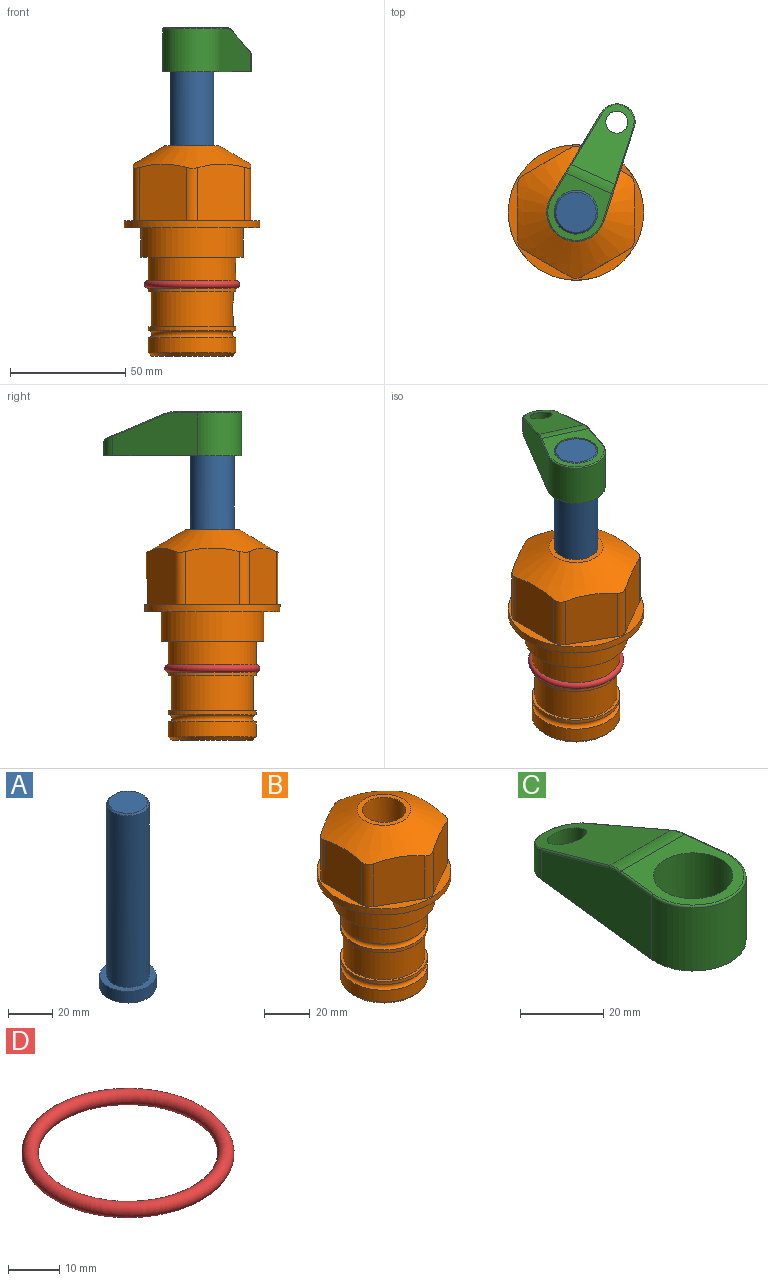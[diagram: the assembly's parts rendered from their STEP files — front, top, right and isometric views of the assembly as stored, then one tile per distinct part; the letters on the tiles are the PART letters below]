
ASSEMBLY  parts=4 mates=2
PART A: 6 faces, bbox 25.4x25.4x101.6 mm
  f0: plane 17.46x17.46mm, normal (0,0,1), area 239.5mm2, adj f5
  f1: plane 25.4x25.4mm, normal (0,0,-1), area 506.7mm2, adj f2
  f2: cylinder r=12.7mm len=25.4mm, axis (0,0,1), area 506.7mm2, adj f1,f3
  f3: plane 25.4x25.4mm, normal (0,0,1), area 221.7mm2, adj f2,f4
  f4: cylinder r=9.53mm len=94.46mm, axis (0,0,1), area 5653mm2, adj f3,f5
  f5: cone r=8.73mm half-angle=45deg, axis (0,0,-1), area 64.4mm2, adj f0,f4
PART B: 36 faces, bbox 58.7x58.7x91.2 mm
  f0: cylinder r=17.78mm len=35.56mm, axis (0,0,1), area 1670.8mm2, adj f23,f24,f31
  f1: cylinder r=19.05mm len=38.1mm, axis (0,0,1), area 1191.9mm2, adj f26,f27,f30
  f2: plane 58.66x58.66mm, normal (0,0,-1), area 1150.6mm2, adj f3,f28
  f3: cylinder r=29.33mm len=58.66mm, axis (0,0,-1), area 585.1mm2, adj f2,f4
  f4: plane 58.66x58.66mm, normal (0,0,1), area 475.9mm2, adj f3,f5,f6,f7,f8,f9,f10,f11
  f5: plane 24.5x20.32mm, normal (-0.5,0.87,0), area 562.8mm2, adj f4,f15,f16,f17
  f6: plane 24.5x20.32mm, normal (0.5,0.87,0), area 562.8mm2, adj f4,f14,f15,f17
  f7: plane 24.5x23.48mm, normal (1,0,0), area 562.8mm2, adj f4,f13,f14,f17
  f8: plane 24.5x20.32mm, normal (0.5,-0.87,0), area 562.8mm2, adj f4,f12,f13,f17
  f9: plane 24.5x20.32mm, normal (-0.5,-0.87,0), area 562.8mm2, adj f4,f11,f12,f17
  f10: plane 24.5x23.48mm, normal (-1,0,0), area 562.8mm2, adj f4,f11,f16,f17
  f11: cylinder r=5.08mm len=23.01mm, axis (0,0,-1), area 121.2mm2, adj f4,f9,f10,f17
  f12: cylinder r=5.08mm len=23.01mm, axis (0,0,-1), area 121.2mm2, adj f4,f8,f9,f17
  f13: cylinder r=5.08mm len=23.01mm, axis (0,0,-1), area 121.2mm2, adj f4,f7,f8,f17
  f14: cylinder r=5.08mm len=23.01mm, axis (0,0,-1), area 121.2mm2, adj f4,f6,f7,f17
  f15: cylinder r=5.08mm len=23.01mm, axis (0,0,-1), area 121.2mm2, adj f4,f5,f6,f17
  f16: cylinder r=5.08mm len=23.01mm, axis (0,0,-1), area 121.2mm2, adj f4,f5,f10,f17
  f17: cone r=11.73mm half-angle=60deg, axis (0,0,-1), area 2071.8mm2, adj f5,f6,f7,f8,f9,f10,f11,f12
  f18: plane 23.46x23.46mm, normal (0,0,1), area 147.4mm2, adj f17,f35
  f19: plane 34.93x34.93mm, normal (0,0,-1), area 958mm2, adj f29
  f20: cylinder r=19.05mm len=38.1mm, axis (0,0,1), area 760.1mm2, adj f21,f29
  f21: torus R=19.05mm, axis (0,0,1), area 565.3mm2, adj f20,f22
  f22: cylinder r=19.05mm len=38.1mm, axis (0,0,1), area 190mm2, adj f21,f23
  f23: plane 38.1x38.1mm, normal (0,0,1), area 146.9mm2, adj f0,f22
  f24: plane 38.1x38.1mm, normal (0,0,-1), area 146.9mm2, adj f0,f25
  f25: cylinder r=19.05mm len=38.1mm, axis (0,0,1), area 190mm2, adj f24,f26
  f26: torus R=19.05mm, axis (0,0,1), area 565.3mm2, adj f1,f25
  f27: plane 44.45x44.45mm, normal (0,0,-1), area 411.7mm2, adj f1,f28
  f28: cylinder r=22.23mm len=44.45mm, axis (0,0,1), area 1773.5mm2, adj f2,f27
  f29: cone r=19.05mm half-angle=45deg, axis (0,0,1), area 257.5mm2, adj f19,f20
  f30: cylinder r=3.17mm len=6.75mm, axis (-1,0,0), area 128mm2, adj f1,f33
  f31: cylinder r=3.17mm len=6.35mm, axis (-1,0,0), area 102.5mm2, adj f0,f33
  f32: plane 25.4x25.4mm, normal (0,0,1), area 506.7mm2, adj f33
  f33: cylinder r=12.7mm len=66.42mm, axis (0,0,-1), area 5236.2mm2, adj f30,f31,f32,f34
  f34: cone r=9.53mm half-angle=30deg, axis (0,0,-1), area 443.4mm2, adj f33,f35
  f35: cylinder r=9.53mm len=19.05mm, axis (0,0,-1), area 849mm2, adj f18,f34
PART C: 44 faces, bbox 27.5x64.5x19.1 mm
  f0: plane 2.3x0.95mm, normal (0,0,-1), area 1mm2, adj f25,f30,f34
  f1: plane 63.5x25.4mm, normal (0,0,-1), area 561.7mm2, adj f2,f3,f4,f5,f6,f7,f19,f20
  f2: cylinder r=12.7mm len=25.4mm, axis (0,0,-1), area 792.2mm2, adj f1,f3,f5,f13
  f3: plane 42.33x18.54mm, normal (0.99,0.11,0), area 647mm2, adj f1,f2,f4,f11,f12,f14
  f4: cylinder r=7.94mm len=15.78mm, axis (0,0,-1), area 158.6mm2, adj f1,f3,f5,f16
  f5: plane 42.33x18.54mm, normal (-0.99,0.11,0), area 647mm2, adj f1,f2,f4,f15,f17,f18
  f6: cylinder r=9.53mm len=19.05mm, axis (0,0,-1), area 1140.1mm2, adj f1,f8
  f7: cylinder r=4.76mm len=10.98mm, axis (0,0,-1), area 276.1mm2, adj f1,f9
  f8: plane 25.83x24.38mm, normal (0,0,1), area 262.2mm2, adj f6,f10,f11,f13,f15
  f9: plane 32.49x20.55mm, normal (0,0.34,0.94), area 489.9mm2, adj f7,f10,f14,f16,f18
  f10: cylinder r=12.7mm len=21.49mm, axis (-1,0,0), area 93.2mm2, adj f8,f9,f12,f17
  f11: cylinder r=0.51mm len=12.34mm, axis (0.11,-0.99,0), area 9.9mm2, adj f3,f8,f12,f13
  f12: bspline ~7.62x1.64mm, area 3.5mm2, adj f3,f10,f11,f14
  f13: torus R=12.19mm, axis (0,0,1), area 33.6mm2, adj f2,f8,f11,f15
  f14: cylinder r=0.51mm len=26.01mm, axis (0.1,-0.93,0.34), area 21.6mm2, adj f3,f9,f12,f16
  f15: cylinder r=0.51mm len=12.34mm, axis (0.11,0.99,0), area 9.9mm2, adj f5,f8,f13,f17
  f16: bspline ~15.78x7.05mm, area 15.7mm2, adj f4,f9,f14,f18
  f17: bspline ~7.62x1.64mm, area 3.5mm2, adj f5,f10,f15,f18
  f18: cylinder r=0.51mm len=26.01mm, axis (0.1,0.93,-0.34), area 21.6mm2, adj f5,f9,f16,f17
  f19: plane 21.6x14.29mm, normal (-0.99,-0.11,0), area 242.6mm2, adj f1,f26,f28,f34,f36,f38
  f20: plane 21.6x14.29mm, normal (0.99,-0.11,0), area 242.6mm2, adj f1,f27,f29,f37,f39,f41
  f21: cylinder r=12.7mm len=14.29mm, axis (0,0,-1), area 173.2mm2, adj f1,f26,f27,f30,f31,f33
  f22: cylinder r=7.94mm len=7.63mm, axis (0,0,-1), area 53.8mm2, adj f1,f28,f29,f42
  f23: plane 2.3x0.95mm, normal (0,0,-1), area 1mm2, adj f25,f33,f37
  f24: plane 17.94x12.32mm, normal (0,-0.34,-0.94), area 191.2mm2, adj f25,f38,f41,f42
  f25: cylinder r=9.53mm len=12.93mm, axis (-1,0,0), area 37.5mm2, adj f0,f23,f24,f31,f36,f39
  f26: cylinder r=1.59mm len=14.29mm, axis (0,0,-1), area 49mm2, adj f1,f19,f21,f32
  f27: cylinder r=1.59mm len=14.29mm, axis (0,0,-1), area 49mm2, adj f1,f20,f21,f35
  f28: cylinder r=1.59mm len=7.28mm, axis (0,0,-1), area 22.1mm2, adj f1,f19,f22,f40
  f29: cylinder r=1.59mm len=7.28mm, axis (0,0,-1), area 22.1mm2, adj f1,f20,f22,f43
  f30: torus R=14.29mm, axis (0,0,1), area 5.8mm2, adj f0,f21,f31,f32
  f31: bspline ~11.06x2.73mm, area 20.8mm2, adj f21,f25,f30,f33
  f32: sphere r=1.59mm, area 5.4mm2, adj f26,f30,f34
  f33: torus R=14.29mm, axis (0,0,1), area 5.8mm2, adj f21,f23,f31,f35
  f34: cylinder r=1.59mm len=1.68mm, axis (-0.11,0.99,0), area 2.4mm2, adj f0,f19,f32,f36
  f35: sphere r=1.59mm, area 5.4mm2, adj f27,f33,f37
  f36: bspline ~5.82x2.33mm, area 7.7mm2, adj f19,f25,f34,f38
  f37: cylinder r=1.59mm len=1.68mm, axis (0.11,0.99,0), area 2.4mm2, adj f20,f23,f35,f39
  f38: cylinder r=1.59mm len=18.33mm, axis (0.1,-0.93,0.34), area 46.7mm2, adj f19,f24,f36,f40
  f39: bspline ~5.82x2.33mm, area 7.7mm2, adj f20,f25,f37,f41
  f40: sphere r=1.59mm, area 3.6mm2, adj f28,f38,f42
  f41: cylinder r=1.59mm len=18.33mm, axis (0.1,0.93,-0.34), area 46.7mm2, adj f20,f24,f39,f43
  f42: bspline ~8.31x1.84mm, area 15.3mm2, adj f22,f24,f40,f43
  f43: sphere r=1.59mm, area 3.6mm2, adj f29,f41,f42
PART D: 1 faces, bbox 44.7x44.7x3.2 mm
  f0: torus R=19.05mm, axis (0,0,1), area 1193.9mm2
PLACE A rot(axis=(0,0,-1),24.4deg) t=(0,0,13.07)mm
PLACE B at identity fixed
PLACE C rot(axis=(0,0,-1),24.4deg) t=(0,0,67.68)mm
PLACE D at identity
MATE fastened C.f2 <-> A.f2  axis (0,0,-1) through (0,0,86.73)mm
MATE cylindrical A.f2 <-> B.f0  axis (0,0,1) through (0,0,38.7)mm
